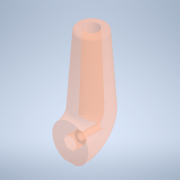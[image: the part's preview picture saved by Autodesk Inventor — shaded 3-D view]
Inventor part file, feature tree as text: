
AUTODESK INVENTOR PART (.ipt)
format: ipt  version: 2020.2 (Build 242310000, 310)  size: 475,648 bytes
history: native  units: in
note: dims shown in document units (in); Inventor stores cm internally (conversion verified against a paired STEP export)
features: sketch x7, plane x5, extrude x3, sweep x2, loft x1, hole x1, fillet x1, chamfer x1, split x1, thicken_offset x1, projected_geometry x1
ambient origin geometry x8: Origin, YZ Plane, XZ Plane, XY Plane, X Axis, Y Axis, Z Axis, Center Point
bodies: Solid23 (feature_tree)
feature tree (24):
  sketch  "Sketch11"  dims[d46=0.8594in d47=0.1322in d48=0.0926in]
  sketch  "Sketch12"  dims[d342=0.002in d343=1.4961in]
  plane  "Work Plane10"
  plane  "Work Plane9"
  sketch  "Sketch17"  dims[d351=4.7244in d352=1.2598in]
  sketch  "Sketch18"  dims[d353=1.2598in d354=0.9449in d360=0.3937in d361=-0.0262in d363=0.3937in d364=0.2362in d365=0.7874in d366=0.5906in d367=90.0deg d368=0.315in d369=0.8108in d370=6.2205in d371=0.1969in d373=0.0394in d374=0.0787in d375=45.0deg d376=0.7874in d377=0.7087in d378=0.0in d379=0.3937in d380=0.6299in d381=-1.1969in d384=2.3622in d385=0.7874in d394=0.0236in d395=0.0394in d396=0.9449in d397=0.1855in d400=1.2598in d401=0.0in d402=90.0deg d403=0.0in d404=90.0deg d405=1.2598in d408=0.0in d409=0.0in d410=0.1969in d382=0.0197in d383=0.0344in]
  plane  "Work Plane8"
  sketch  "Sketch16"  dims[d0=0.002in d1=4.7244in]
  extrude  "Extrusion25"  Depth=0.0926in
  sweep  "Sweep7"
  extrude  "Extrusion26"  Depth=2.5197in
  loft  "Loft1"
  sweep  "Sweep11"
  hole  "Hole1"  [1 undecoded]
  extrude  "Extrusion27"  Depth=1.2598in
  fillet  "Fillet28"  Radius=0.3937in
  chamfer  "Chamfer1"  Distance=6.2205in
  plane  "Work Plane6"
  plane  "Work Plane7"
  split  "Split6"
  thicken_offset  "Thicken20"
  sketch  "Sketch14"  dims[d344=90.0deg d345=2.5197in]
  projected_geometry  "Projected Loop5"
  sketch  "Sketch15"  dims[d346=0.3937in d347=0.0in d348=0.0in d349=0.0in]
note: 1 required parameter value undecoded (feature->parameter linkage not recoverable at this tier; creation-order binding heuristic only, values carry confidence <= 0.55)
